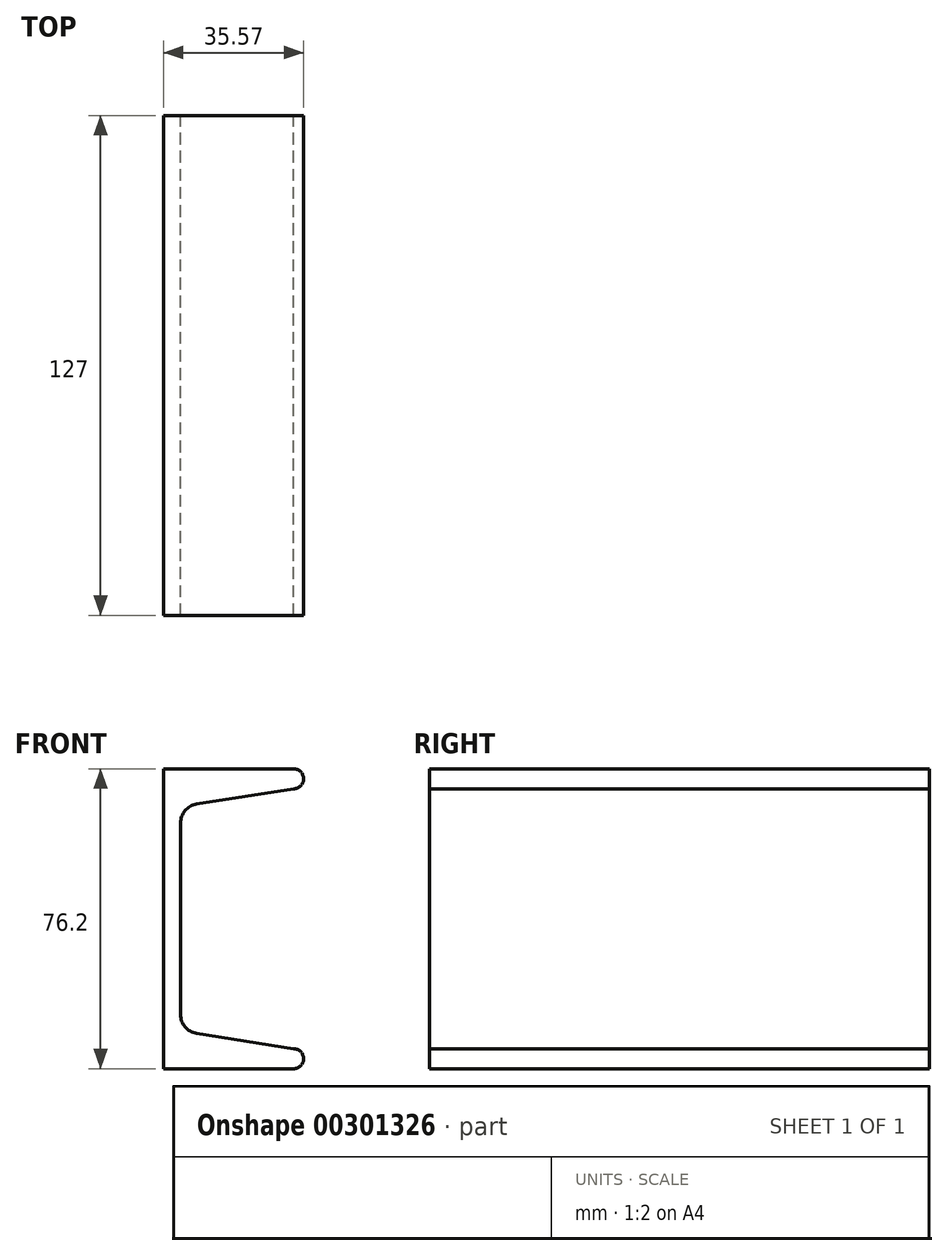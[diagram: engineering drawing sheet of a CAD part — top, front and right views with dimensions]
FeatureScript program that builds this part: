
annotation { "Feature Type Name" : "Feature", "Feature Type Description" : "" }
export const myFeature = defineFeature(function(context is Context, id is Id, definition is map)
    precondition{}
    {
        {
            var Q0;
            Q0=qCreatedBy(makeId("Front.planeOp"),FACE);
            var sketch = newSketch(context, id + "F0", { "sketchPlane" : qUnion([Q0])});
            skLineSegment(sketch, "E0", {"start": v(4.32, 24.33) * mm, "end": v(4.32, 0) * mm});
            skLineSegment(sketch, "E1", {"start": v(0, 38.1) * mm, "end": v(33.03, 38.1) * mm});
            skLineSegment(sketch, "E2", {"start": v(33.03, 38.1) * mm, "end": v(65.1, 38.1) * mm, "construction": true});
            skLineSegment(sketch, "E3", {"start": v(65.1, 38.1) * mm, "end": v(33.03, 33.02) * mm, "construction": true});
            skArc(sketch, "E4", {"start": v(33.03, 33.02) * mm, "mid": v(35.57, 35.56) * mm, "end": v(33.03, 38.1) * mm});
            skLineSegment(sketch, "E5", {"start": v(0, 38.1) * mm, "end": v(0, 0) * mm});
            skLineSegment(sketch, "E6", {"start": v(33.03, 33.02) * mm, "end": v(8.41, 29.12) * mm});
            skArc(sketch, "E7", {"start": v(8.41, 29.12) * mm, "mid": v(5.48, 27.48) * mm, "end": v(4.32, 24.33) * mm});
            skLineSegment(sketch, "E8.MirrorCS", {"start": v(4.32, -24.33) * mm, "end": v(4.32, 0) * mm});
            skLineSegment(sketch, "E9.MirrorCS", {"start": v(0, -38.1) * mm, "end": v(33.03, -38.1) * mm});
            skArc(sketch, "E10.MirrorCS", {"start": v(8.41, -29.12) * mm, "mid": v(5.48, -27.48) * mm, "end": v(4.32, -24.33) * mm});
            skLineSegment(sketch, "E11.MirrorCS", {"start": v(0, -38.1) * mm, "end": v(0, 0) * mm});
            skLineSegment(sketch, "E12.MirrorCS", {"start": v(33.03, -33.02) * mm, "end": v(8.41, -29.12) * mm});
            skArc(sketch, "E13.MirrorCS", {"start": v(33.03, -33.02) * mm, "mid": v(35.57, -35.56) * mm, "end": v(33.03, -38.1) * mm});
            skSolve(sketch);
        }
        {
            var Q0;
            Q0=makeQuery(id+"F0.imprint","IMPRINT",FACE,{"disambiguationData":[TD([[makeQuery(id+"F0.imprint","IMPRINT",EDGE,{"derivedFrom":sQuery(id+"F0.wireOp",EDGE,"E0")}),-1.0]])]});
            extrude(context, id + "F1", {"entities" : qUnion([Q0]), "depth" : 127 * mm});
        }
    });
